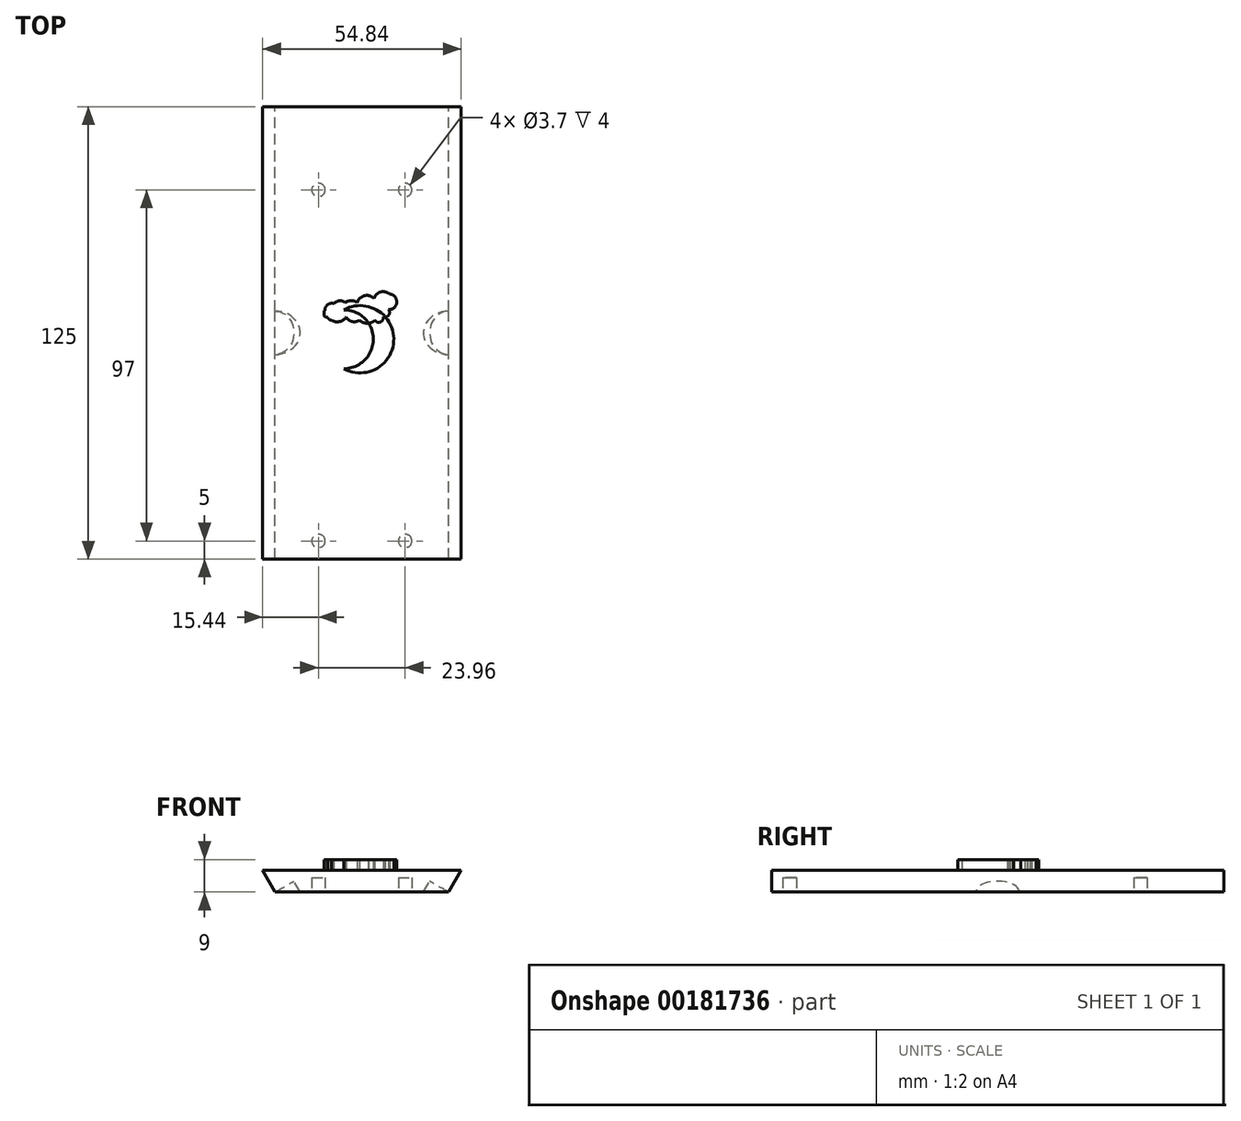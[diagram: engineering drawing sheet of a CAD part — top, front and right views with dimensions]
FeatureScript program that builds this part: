
annotation { "Feature Type Name" : "Feature", "Feature Type Description" : "" }
export const myFeature = defineFeature(function(context is Context, id is Id, definition is map)
    precondition{}
    {
        {
            var Q0;
            Q0=qCreatedBy(makeId("Front.planeOp"),FACE);
            var sketch = newSketch(context, id + "F0", { "sketchPlane" : qUnion([Q0])});
            skCircle(sketch, "E0.cCircle", {"center": v(0, 0) * mm, "radius": 47.5 * mm, "construction": true});
            skLineSegment(sketch, "E0.0", {"start": v(-27.42, -47.5) * mm, "end": v(-54.85, 0) * mm});
            skLineSegment(sketch, "E0.1", {"start": v(-54.85, 0) * mm, "end": v(-27.42, 47.5) * mm});
            skLineSegment(sketch, "E0.2", {"start": v(-27.42, 47.5) * mm, "end": v(27.42, 47.5) * mm});
            skLineSegment(sketch, "E0.3", {"start": v(27.42, 47.5) * mm, "end": v(54.85, 0) * mm});
            skLineSegment(sketch, "E0.4", {"start": v(54.85, 0) * mm, "end": v(27.42, -47.5) * mm});
            skLineSegment(sketch, "E0.5", {"start": v(27.42, -47.5) * mm, "end": v(-27.42, -47.5) * mm});
            skPoint(sketch, "E0.0.midPoint", {"position": v(-41.14, -23.75) * mm});
            skCircle(sketch, "E1.cCircle", {"center": v(0, 0) * mm, "radius": 41.5 * mm, "construction": true});
            skLineSegment(sketch, "E1.0", {"start": v(-23.96, -41.5) * mm, "end": v(-47.92, 0) * mm});
            skLineSegment(sketch, "E1.1", {"start": v(-47.92, 0) * mm, "end": v(-23.96, 41.5) * mm});
            skLineSegment(sketch, "E1.2", {"start": v(-23.96, 41.5) * mm, "end": v(23.96, 41.5) * mm});
            skLineSegment(sketch, "E1.3", {"start": v(23.96, 41.5) * mm, "end": v(47.92, 0) * mm});
            skLineSegment(sketch, "E1.4", {"start": v(47.92, 0) * mm, "end": v(23.96, -41.5) * mm});
            skLineSegment(sketch, "E1.5", {"start": v(23.96, -41.5) * mm, "end": v(-23.96, -41.5) * mm});
            skPoint(sketch, "E1.0.midPoint", {"position": v(-35.94, -20.75) * mm});
            skLineSegment(sketch, "E2", {"start": v(27.42, 47.5) * mm, "end": v(23.96, 41.5) * mm});
            skLineSegment(sketch, "E3", {"start": v(-27.42, 47.5) * mm, "end": v(-23.96, 41.5) * mm});
            skSolve(sketch);
        }
        {
            var Q0;
            Q0=makeQuery(id+"F0.imprint","IMPRINT",FACE,{"disambiguationData":[TD([[makeQuery(id+"F0.imprint","IMPRINT",EDGE,{"derivedFrom":sQuery(id+"F0.wireOp",EDGE,"E0.2")}),-1.0]])]});
            extrude(context, id + "F1", {"entities" : qUnion([Q0]), "depth" : 125 * mm});
        }
        {
            var Q0;
            Q0=makeQuery(id+"F1.opExtrude","SWEPT_FACE",FACE,{"disambiguationData":[OSD([sQuery(id+"F0.wireOp",EDGE,"E1.2")])]});
            var sketch = newSketch(context, id + "F2", { "sketchPlane" : qUnion([Q0])});
            skPoint(sketch, "E4", {"position": v(0, 125) * mm});
            skPoint(sketch, "E5", {"position": v(0, 120) * mm});
            skLineSegment(sketch, "E6", {"start": v(0, 120) * mm, "end": v(-23.96, 120) * mm});
            skPoint(sketch, "E7", {"position": v(-11.98, 120) * mm});
            skCircle(sketch, "E8", {"center": v(-11.98, 120) * mm, "radius": 1.85 * mm});
            skCircle(sketch, "E9.MirrorC", {"center": v(11.98, 120) * mm, "radius": 1.85 * mm});
            skPoint(sketch, "E10", {"position": v(0, 23) * mm});
            skLineSegment(sketch, "E11", {"start": v(0, 23) * mm, "end": v(-23.96, 23) * mm});
            skPoint(sketch, "E12", {"position": v(-11.98, 23) * mm});
            skCircle(sketch, "E13", {"center": v(-11.98, 23) * mm, "radius": 1.85 * mm});
            skCircle(sketch, "E14.MirrorC", {"center": v(11.98, 23) * mm, "radius": 1.85 * mm});
            skSolve(sketch);
        }
        {
            var Q0;
            Q0=qSketchRegion(id+"F2",true);
            extrude(context, id + "F3", {"entities" : qUnion([Q0]), "operationType" : NewBodyOperationType.REMOVE, "oppositeDirection" : true, "depth" : 4 * mm});
        }
        {
            var Q0;
            Q0=makeQuery(id+"F1.opExtrude","SWEPT_FACE",FACE,{"disambiguationData":[OSD([sQuery(id+"F0.wireOp",EDGE,"E0.2")])]});
            var sketch = newSketch(context, id + "F4", { "sketchPlane" : qUnion([Q0])});
            skPoint(sketch, "E15", {"position": v(-23.96, -62.5) * mm});
            skPoint(sketch, "E16", {"position": v(0, -90) * mm});
            skPoint(sketch, "E17", {"position": v(0, -62.5) * mm});
            skLineSegment(sketch, "E18.MirrorCS", {"start": v(6.47, -58.14) * mm, "end": v(6.47, -58.09) * mm});
            skArc(sketch, "E19.MirrorCS", {"start": v(-9.45, -58.15) * mm, "mid": v(-9.05, -58.78) * mm, "end": v(-8.35, -59.03) * mm});
            skLineSegment(sketch, "E20.MirrorCS", {"start": v(1.94, -59.82) * mm, "end": v(1.82, -59.78) * mm});
            skArc(sketch, "E21.MirrorCS", {"start": v(3.6, -59.02) * mm, "mid": v(5.17, -59.5) * mm, "end": v(5.92, -58.03) * mm});
            skArc(sketch, "E22.MirrorCS", {"start": v(3.43, -53.02) * mm, "mid": v(0.77, -52.23) * mm, "end": v(-1.23, -54.16) * mm});
            skArc(sketch, "E23.MirrorCS", {"start": v(-10.18, -56.27) * mm, "mid": v(-10.61, -57.51) * mm, "end": v(-9.45, -58.15) * mm});
            skArc(sketch, "E24.MirrorCS", {"start": v(-7.75, -54.4) * mm, "mid": v(-9.45, -54.7) * mm, "end": v(-10.18, -56.27) * mm});
            skArc(sketch, "E25.MirrorCS", {"start": v(7.57, -51.73) * mm, "mid": v(5.14, -51.22) * mm, "end": v(3.43, -53.02) * mm});
            skArc(sketch, "E26.MirrorCS", {"start": v(7.38, -56.09) * mm, "mid": v(9.65, -54) * mm, "end": v(7.57, -51.73) * mm});
            skArc(sketch, "E27.MirrorCS", {"start": v(-0.64, -59.02) * mm, "mid": v(1.48, -59.85) * mm, "end": v(3.6, -59.02) * mm});
            skArc(sketch, "E28.MirrorCS", {"start": v(-1.23, -54.16) * mm, "mid": v(-2.88, -53.58) * mm, "end": v(-4.52, -54.16) * mm});
            skArc(sketch, "E29.MirrorCS", {"start": v(5.92, -58.03) * mm, "mid": v(7.43, -57.65) * mm, "end": v(7.38, -56.09) * mm});
            skArc(sketch, "E30.MirrorCS", {"start": v(-8.35, -59.03) * mm, "mid": v(-6.17, -59.4) * mm, "end": v(-4.35, -58.15) * mm});
            skArc(sketch, "E31.MirrorCS", {"start": v(-4.52, -54.16) * mm, "mid": v(-6.18, -53.64) * mm, "end": v(-7.75, -54.4) * mm});
            skArc(sketch, "E32.MirrorCS", {"start": v(-4.35, -58.15) * mm, "mid": v(-2.68, -59.37) * mm, "end": v(-0.64, -59.02) * mm});
            skLineSegment(sketch, "E33.MirrorCS", {"start": v(9.42, -54.26) * mm, "end": v(-10.36, -54.26) * mm});
            skLineSegment(sketch, "E34.MirrorCS", {"start": v(-0.47, -64.26) * mm, "end": v(-9.48, -64.26) * mm});
            skPoint(sketch, "E35.MirrorP", {"position": v(1.3, -55.2) * mm});
            skLineSegment(sketch, "E36.MirrorCS", {"start": v(9.42, -64.26) * mm, "end": v(-10.36, -64.26) * mm});
            skPoint(sketch, "E37.MirrorP", {"position": v(-0.47, -74.26) * mm});
            skArc(sketch, "E38.MirrorCS", {"start": v(-4.96, -72.4) * mm, "mid": v(8.82, -64.26) * mm, "end": v(-4.96, -56.12) * mm});
            skLineSegment(sketch, "E39.MirrorCS", {"start": v(9.42, -74.26) * mm, "end": v(-10.36, -74.26) * mm});
            skPoint(sketch, "E40.MirrorP", {"position": v(-4.98, -64.26) * mm});
            skPoint(sketch, "E41.MirrorP", {"position": v(9.42, -64.26) * mm});
            skPoint(sketch, "E42.MirrorP", {"position": v(-0.47, -54.26) * mm});
            skArc(sketch, "E43.MirrorCS", {"start": v(-4.96, -72.4) * mm, "mid": v(3.16, -64.26) * mm, "end": v(-4.96, -56.12) * mm});
            skLineSegment(sketch, "E44.MirrorCS", {"start": v(-10.36, -74.26) * mm, "end": v(-10.36, -54.26) * mm});
            skLineSegment(sketch, "E45.MirrorCS", {"start": v(9.42, -74.26) * mm, "end": v(9.42, -54.26) * mm});
            skSolve(sketch);
        }
        {
            var Q0;
            {var subQ0=sQuery(id+"F4.wireOp",EDGE,"E38.MirrorCS");var subQ1=sQuery(id+"F4.wireOp",EDGE,"E36.MirrorCS");var subQ2=makeQuery(id+"F4.imprint","INTERSECT",VERTEX,{"derivedFrom":[subQ1,subQ0]});Q0=makeQuery(id+"F4.imprint","IMPRINT",FACE,{"disambiguationData":[TD([[makeQuery(id+"F4.imprint","IMPRINT",EDGE,{"disambiguationData":[TD([[subQ2,-1.0]])],"derivedFrom":subQ1}),1.0]])]});}
            var Q1;
            {var subQ2=sQuery(id+"F4.wireOp",EDGE,"E21.MirrorCS");Q1=makeQuery(id+"F4.imprint","IMPRINT",FACE,{"disambiguationData":[TD([[makeQuery(id+"F4.imprint","IMPRINT",EDGE,{"derivedFrom":subQ2}),-1.0]])]});}
            var Q2;
            {var subQ0=sQuery(id+"F4.wireOp",EDGE,"E19.MirrorCS");Q2=makeQuery(id+"F4.imprint","IMPRINT",FACE,{"disambiguationData":[TD([[makeQuery(id+"F4.imprint","IMPRINT",EDGE,{"derivedFrom":subQ0}),1.0]])]});}
            var Q3;
            Q3=makeQuery(id+"F4.imprint","IMPRINT",FACE,{"disambiguationData":[TD([[makeQuery(id+"F4.imprint","IMPRINT",EDGE,{"derivedFrom":sQuery(id+"F4.wireOp",EDGE,"E22.MirrorCS")}),1.0]])]});
            var Q4;
            {var subQ0=sQuery(id+"F4.wireOp",EDGE,"E20.MirrorCS");Q4=makeQuery(id+"F4.imprint","IMPRINT",FACE,{"disambiguationData":[TD([[makeQuery(id+"F4.imprint","IMPRINT",EDGE,{"derivedFrom":subQ0}),1.0]])]});}
            var Q5;
            {var subQ0=sQuery(id+"F4.wireOp",EDGE,"E18.MirrorCS");Q5=makeQuery(id+"F4.imprint","IMPRINT",FACE,{"disambiguationData":[TD([[makeQuery(id+"F4.imprint","IMPRINT",EDGE,{"derivedFrom":subQ0}),-1.0]])]});}
            extrude(context, id + "F5", {"entities" : qUnion([Q0, Q1, Q2, Q3, Q4, Q5]), "operationType" : NewBodyOperationType.ADD, "depth" : 3 * mm});
        }
        {
            var Q0;
            Q0=makeQuery(id+"F1.opExtrude","SWEPT_EDGE",EDGE,{"disambiguationData":[OSD([sQuery(id+"F0.wireOp",EDGE,"E1.1"),sQuery(id+"F0.wireOp",EDGE,"E1.2"),sQuery(id+"F0.wireOp",EDGE,"E3")])]});
            cPlane(context, id + "F6", {"entities" : qUnion([Q0]), "cplaneType" : CPlaneType.LINE_ANGLE, "offset" : 25 * mm, "angle" : 150 * degree, "width" : 150 * mm, "height" : 150 * mm});
        }
        {
            var Q0;
            Q0=qCreatedBy(id+"F6.planeOp",FACE);
            var sketch = newSketch(context, id + "F7", { "sketchPlane" : qUnion([Q0])});
            skCircle(sketch, "E46", {"center": v(0, 62.5) * mm, "radius": 6 * mm});
            skSolve(sketch);
        }
        {
            var Q0;
            Q0=qSketchRegion(id+"F7",true);
            extrude(context, id + "F8", {"entities" : qUnion([Q0]), "operationType" : NewBodyOperationType.REMOVE, "depth" : 25 * mm});
        }
        {
            var Q0;
            Q0=makeQuery(id+"F1.opExtrude","SWEPT_EDGE",EDGE,{"disambiguationData":[OSD([sQuery(id+"F0.wireOp",EDGE,"E1.2"),sQuery(id+"F0.wireOp",EDGE,"E1.3"),sQuery(id+"F0.wireOp",EDGE,"E2")])]});
            cPlane(context, id + "F9", {"entities" : qUnion([Q0]), "cplaneType" : CPlaneType.LINE_ANGLE, "offset" : 25 * mm, "angle" : 30 * degree, "width" : 150 * mm, "height" : 150 * mm});
        }
        {
            var Q0;
            Q0=qCreatedBy(id+"F9.planeOp",FACE);
            var sketch = newSketch(context, id + "F10", { "sketchPlane" : qUnion([Q0])});
            skCircle(sketch, "E47", {"center": v(0, -62.5) * mm, "radius": 6 * mm});
            skSolve(sketch);
        }
        {
            var Q0;
            Q0=qSketchRegion(id+"F10",true);
            extrude(context, id + "F11", {"entities" : qUnion([Q0]), "operationType" : NewBodyOperationType.REMOVE, "oppositeDirection" : true, "depth" : 25 * mm});
        }
    });
